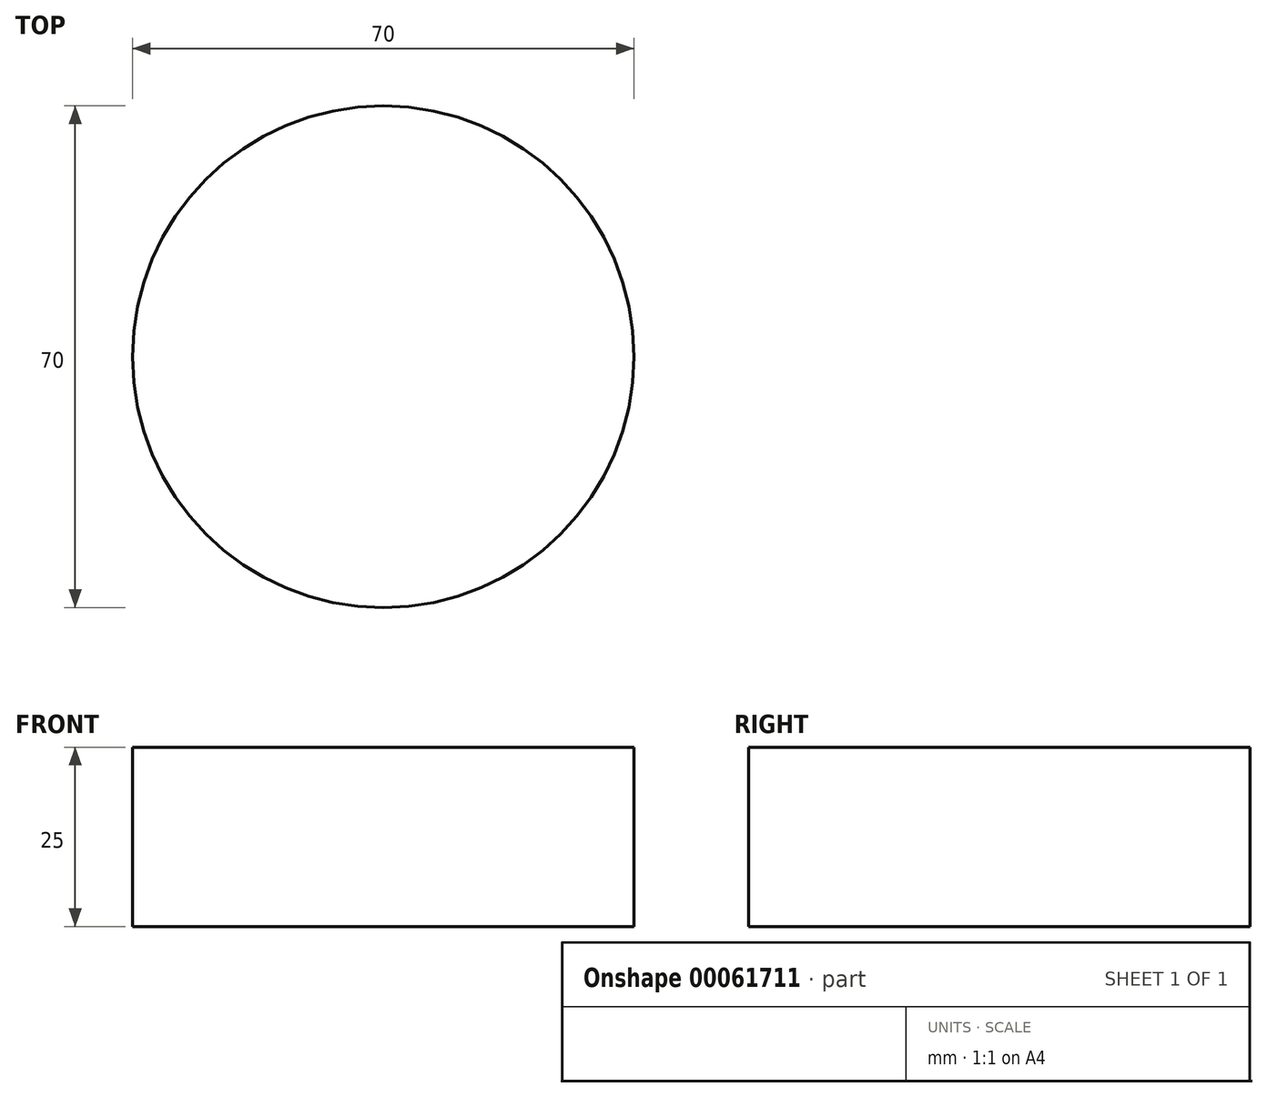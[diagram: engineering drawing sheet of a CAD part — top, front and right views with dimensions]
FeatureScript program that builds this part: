
annotation { "Feature Type Name" : "Feature", "Feature Type Description" : "" }
export const myFeature = defineFeature(function(context is Context, id is Id, definition is map)
    precondition{}
    {
        {
            var Q0;
            Q0=qCreatedBy(makeId("Top.planeOp"),FACE);
            var sketch = newSketch(context, id + "F0", { "sketchPlane" : qUnion([Q0])});
            skCircle(sketch, "E0", {"center": v(0, 0) * mm, "radius": 35 * mm});
            skSolve(sketch);
        }
        {
            var Q0;
            Q0 = qSketchRegion(id + "F0", true);
            extrude(context, id + "F1", {"entities" : qUnion([Q0]), "depth" : 25 * mm});
        }
    });
